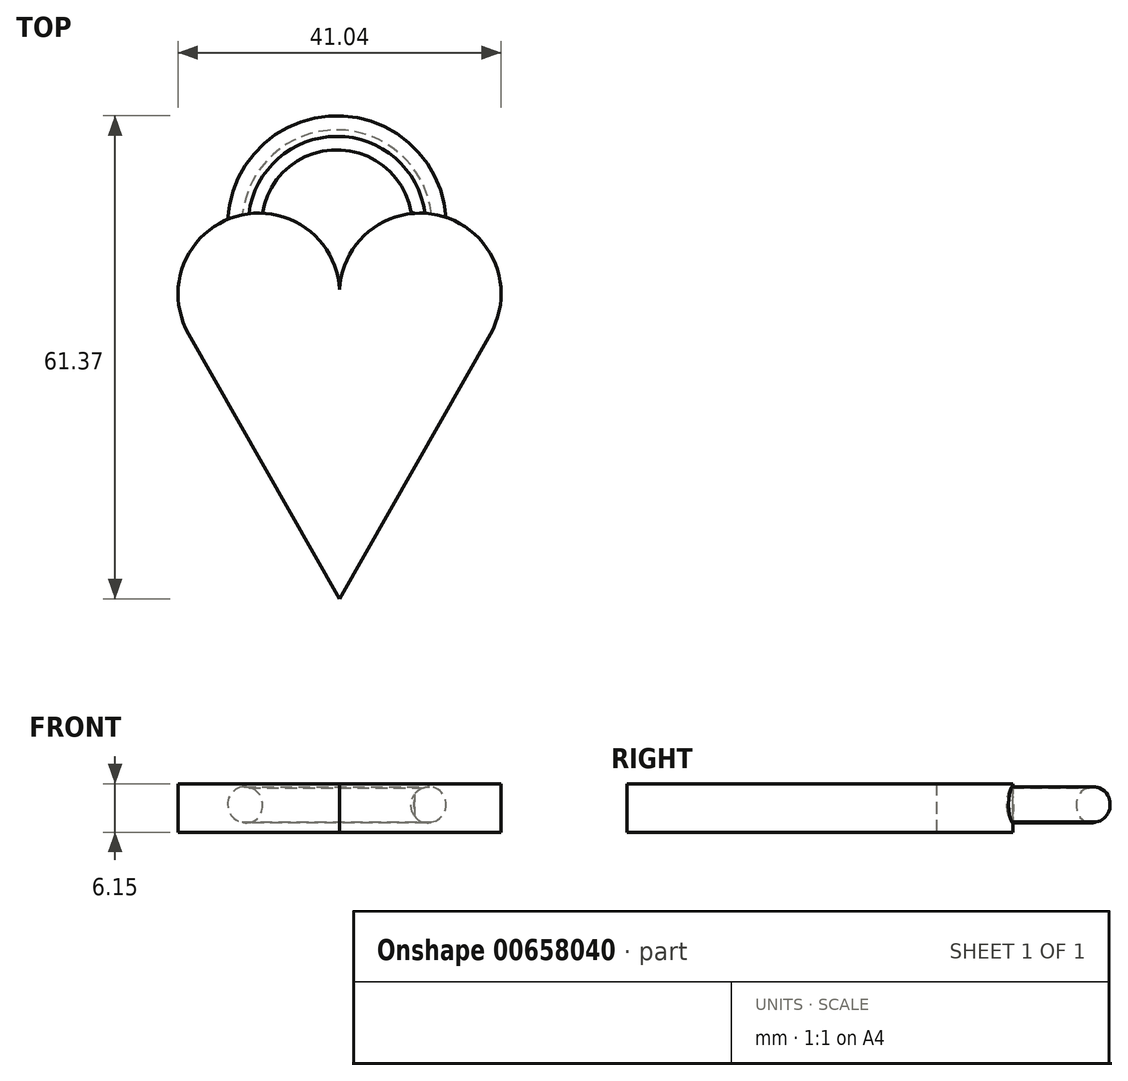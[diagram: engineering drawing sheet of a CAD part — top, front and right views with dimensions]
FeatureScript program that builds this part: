
annotation { "Feature Type Name" : "Feature", "Feature Type Description" : "" }
export const myFeature = defineFeature(function(context is Context, id is Id, definition is map)
    precondition{}
    {
        {
            var Q0;
            Q0=qCreatedBy(makeId("Top.planeOp"),FACE);
            var sketch = newSketch(context, id + "F0", { "sketchPlane" : qUnion([Q0])});
            skCircle(sketch, "E0", {"center": v(-51.54, -21.88) * mm, "radius": 8.48 * mm});
            skLineSegment(sketch, "E1", {"start": v(-43.07, -21.42) * mm, "end": v(-43.07, 0) * mm});
            skCircle(sketch, "E2.MirrorC", {"center": v(-34.6, -21.88) * mm, "radius": 8.48 * mm});
            skLineSegment(sketch, "E3", {"start": v(-43.07, -21.42) * mm, "end": v(-43.07, -53.9) * mm});
            skLineSegment(sketch, "E4", {"start": v(-43.07, -53.9) * mm, "end": v(-58.92, -26.09) * mm});
            skLineSegment(sketch, "E5", {"start": v(-43.07, -53.9) * mm, "end": v(-27.23, -26.09) * mm});
            skSolve(sketch);
        }
        {
            var Q0;
            Q0 = qSketchRegion(id + "F0", true);
            extrude(context, id + "F1", {"entities" : qUnion([Q0]), "depth" : 5.08 * mm, "offsetDistance" : 25.4 * mm});
        }
        {
            var Q0;
            Q0=qCreatedBy(makeId("Top.planeOp"),FACE);
            cPlane(context, id + "F2", {"entities" : qUnion([Q0]), "cplaneType" : CPlaneType.OFFSET, "offset" : 3.17 * mm, "width" : 152.4 * mm, "height" : 152.4 * mm});
        }
        {
            var Q0;
            Q0=qCreatedBy(makeId("Front.planeOp"),FACE);
            cPlane(context, id + "F3", {"entities" : qUnion([Q0]), "cplaneType" : CPlaneType.OFFSET, "offset" : 19.05 * mm, "width" : 152.4 * mm, "height" : 152.4 * mm});
        }
        {
            var Q0;
            Q0=qCreatedBy(id+"F3.planeOp",FACE);
            var sketch = newSketch(context, id + "F4", { "sketchPlane" : qUnion([Q0])});
            skCircle(sketch, "E6", {"center": v(-34.57, 2.9) * mm, "radius": 1.85 * mm});
            skCircle(sketch, "E7", {"center": v(-51.78, 2.83) * mm, "radius": 1.85 * mm});
            skSolve(sketch);
        }
        {
            var Q0;
            Q0=qCreatedBy(id+"F2.planeOp",FACE);
            var sketch = newSketch(context, id + "F5", { "sketchPlane" : qUnion([Q0])});
            skArc(sketch, "E8", {"start": v(-34.67, -16.62) * mm, "mid": v(-43.2, -5.77) * mm, "end": v(-52.08, -16.32) * mm});
            skSolve(sketch);
        }
        {
            var Q0;
            Q0 = qSketchRegion(id + "F4", true);
            var Q1;
            Q1=sQuery(id+"F5.wireOp",EDGE,"E8");
            sweep(context, id + "F6", {"operationType" : NewBodyOperationType.ADD, "profiles" : qUnion([Q0]), "path" : qUnion([Q1])});
        }
        {
            var Q0;
            Q0=qCreatedBy(id+"F2.planeOp",FACE);
            var sketch = newSketch(context, id + "F7", { "sketchPlane" : qUnion([Q0])});
            skCircle(sketch, "E9", {"center": v(18.38, 60.26) * mm, "radius": 11.1 * mm});
            skLineSegment(sketch, "E10", {"start": v(29.48, 59.91) * mm, "end": v(29.98, 76.15) * mm});
            skCircle(sketch, "E11.MirrorC", {"center": v(40.58, 59.57) * mm, "radius": 11.1 * mm});
            skLineSegment(sketch, "E12", {"start": v(29.48, 59.91) * mm, "end": v(29.48, 16.03) * mm});
            skLineSegment(sketch, "E13", {"start": v(29.48, 16.03) * mm, "end": v(8.59, 55.01) * mm});
            skLineSegment(sketch, "E14", {"start": v(29.48, 16.03) * mm, "end": v(50.74, 55.01) * mm});
            skSolve(sketch);
        }
        {
            var Q0;
            Q0 = qSketchRegion(id + "F7", true);
            extrude(context, id + "F8", {"entities" : qUnion([Q0]), "depth" : 5.08 * mm, "offsetDistance" : 25.4 * mm});
        }
        {
            var Q0;
            Q0=makeQuery(id+"F8.opExtrude","SWEPT_BODY",BODY,{"disambiguationData":[OSD([sQuery(id+"F7.wireOp",EDGE,"E9"),sQuery(id+"F7.wireOp",EDGE,"E11.MirrorC"),sQuery(id+"F7.wireOp",EDGE,"E13"),sQuery(id+"F7.wireOp",EDGE,"E14")])]});
            var Q1;
            Q1=makeQuery(id+"F8.opExtrude","CAP_VERTEX",VERTEX,{"disambiguationData":[OSD([sQuery(id+"F7.wireOp",EDGE,"E12"),sQuery(id+"F7.wireOp",EDGE,"E13"),sQuery(id+"F7.wireOp",EDGE,"E14")])],"isStart":false});
            transform(context, id + "F9", {"entities" : qUnion([Q0]), "transformType" : TransformType.SCALE_UNIFORMLY, "scale" : 1, "scalePoint" : qUnion([Q1]), "makeCopy" : false});
        }
        {
            var Q0;
            Q0=makeQuery(id+"F1.opExtrude","SWEPT_BODY",BODY,{"disambiguationData":[OSD([sQuery(id+"F0.wireOp",EDGE,"E0"),sQuery(id+"F0.wireOp",EDGE,"E2.MirrorC"),sQuery(id+"F0.wireOp",EDGE,"E4"),sQuery(id+"F0.wireOp",EDGE,"E5")])]});
            var Q1;
            Q1=sQuery(id+"F0.wireOp",VERTEX,"E5.start");
            transform(context, id + "F10", {"entities" : qUnion([Q0]), "transformType" : TransformType.SCALE_UNIFORMLY, "scale" : 1.1, "scalePoint" : qUnion([Q1]), "makeCopy" : false});
        }
        {
            var Q0;
            Q0=makeQuery(id+"F1.opExtrude","SWEPT_BODY",BODY,{"disambiguationData":[OSD([sQuery(id+"F0.wireOp",EDGE,"E0"),sQuery(id+"F0.wireOp",EDGE,"E2.MirrorC"),sQuery(id+"F0.wireOp",EDGE,"E4"),sQuery(id+"F0.wireOp",EDGE,"E5")])]});
            var Q1;
            Q1=sQuery(id+"F0.wireOp",VERTEX,"E5.start");
            transform(context, id + "F11", {"entities" : qUnion([Q0]), "transformType" : TransformType.SCALE_UNIFORMLY, "scale" : 1.1, "scalePoint" : qUnion([Q1]), "makeCopy" : false});
        }
        {
            var Q0;
            Q0=makeQuery(id+"F8.opExtrude","SWEPT_BODY",BODY,{"disambiguationData":[OSD([sQuery(id+"F7.wireOp",EDGE,"E9"),sQuery(id+"F7.wireOp",EDGE,"E11.MirrorC"),sQuery(id+"F7.wireOp",EDGE,"E13"),sQuery(id+"F7.wireOp",EDGE,"E14")])]});
            deleteBodies(context, id + "F12", {"entities" : qUnion([Q0])});
        }
    });
